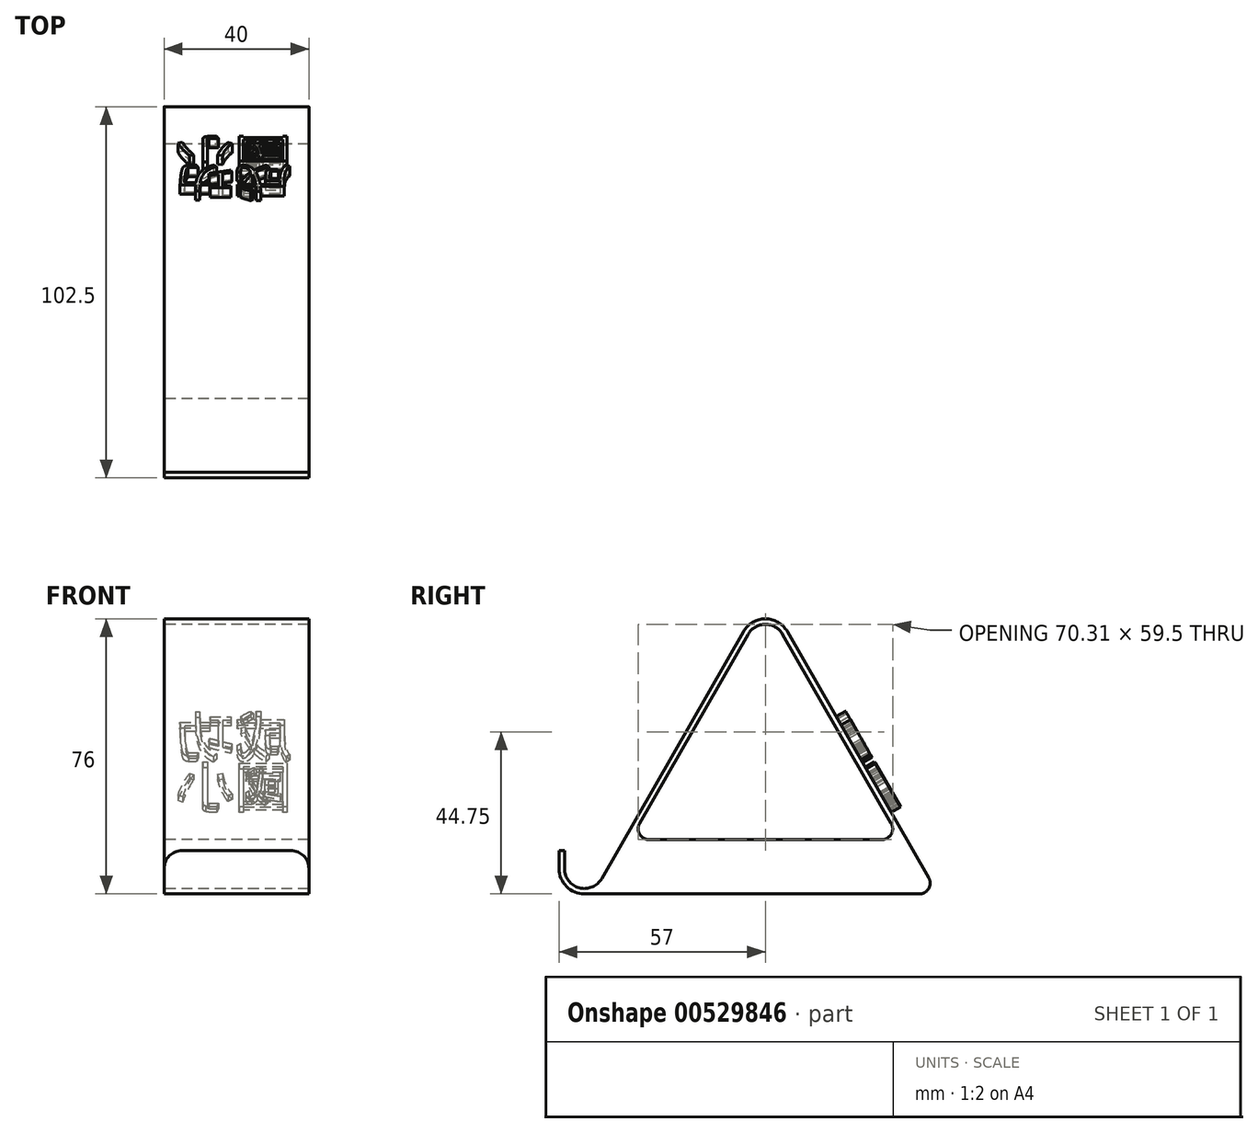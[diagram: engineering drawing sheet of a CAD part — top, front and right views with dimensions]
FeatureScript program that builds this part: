
annotation { "Feature Type Name" : "Feature", "Feature Type Description" : "" }
export const myFeature = defineFeature(function(context is Context, id is Id, definition is map)
    precondition{}
    {
        {
            var Q0;
            Q0=qCreatedBy(makeId("Right.planeOp"),FACE);
            var sketch = newSketch(context, id + "F0", { "sketchPlane" : qUnion([Q0])});
            skArc(sketch, "E0", {"start": v(-7, 0) * mm, "mid": v(-4.95, -4.95) * mm, "end": v(0, -7) * mm});
            skArc(sketch, "E1", {"start": v(54.77, 64.74) * mm, "mid": v(50, 67.5) * mm, "end": v(45.23, 64.74) * mm});
            skLineSegment(sketch, "E2", {"start": v(15.24, 12.5) * mm, "end": v(45.23, 64.74) * mm});
            skLineSegment(sketch, "E3", {"start": v(50, 62) * mm, "end": v(50, -35.11) * mm, "construction": true});
            skLineSegment(sketch, "E4.0.MirrorCS", {"start": v(84.76, 12.5) * mm, "end": v(54.77, 64.74) * mm});
            skLineSegment(sketch, "E5", {"start": v(0, -7) * mm, "end": v(125.8, -7) * mm, "construction": true});
            skLineSegment(sketch, "E6", {"start": v(-7, 0) * mm, "end": v(-7, 5) * mm});
            skLineSegment(sketch, "E7.0", {"start": v(-5.5, 0) * mm, "end": v(-5.5, 5) * mm});
            skArc(sketch, "E7.1", {"start": v(-5.5, 0) * mm, "mid": v(-1.42, -5.31) * mm, "end": v(4.77, -2.74) * mm});
            skLineSegment(sketch, "E7.2", {"start": v(4.77, -2.74) * mm, "end": v(43.93, 65.48) * mm});
            skArc(sketch, "E7.3", {"start": v(56.07, 65.48) * mm, "mid": v(50, 69) * mm, "end": v(43.93, 65.48) * mm});
            skLineSegment(sketch, "E7.4", {"start": v(95.1, -2.5) * mm, "end": v(56.07, 65.48) * mm});
            skLineSegment(sketch, "E8", {"start": v(-7, 5) * mm, "end": v(-5.5, 5) * mm});
            skLineSegment(sketch, "E9", {"start": v(0, -7) * mm, "end": v(92.5, -7) * mm});
            skLineSegment(sketch, "E10.0", {"start": v(17.84, 8) * mm, "end": v(82.16, 8) * mm});
            skPoint(sketch, "E11.visualSharp", {"position": v(12.66, 8) * mm});
            skArc(sketch, "E11.filletArc", {"start": v(15.24, 12.5) * mm, "mid": v(15.25, 9.5) * mm, "end": v(17.84, 8) * mm});
            skPoint(sketch, "E12.visualSharp", {"position": v(87.34, 8) * mm});
            skArc(sketch, "E12.filletArc", {"start": v(82.16, 8) * mm, "mid": v(84.75, 9.5) * mm, "end": v(84.76, 12.5) * mm});
            skPoint(sketch, "E13.visualSharp", {"position": v(97.68, -7) * mm});
            skArc(sketch, "E13.filletArc", {"start": v(92.5, -7) * mm, "mid": v(95.1, -5.5) * mm, "end": v(95.1, -2.5) * mm});
            skSolve(sketch);
        }
        {
            var Q0;
            Q0=makeQuery(id+"F0.imprint","IMPRINT",FACE,{"disambiguationData":[TD([[makeQuery(id+"F0.imprint","IMPRINT",EDGE,{"derivedFrom":sQuery(id+"F0.wireOp",EDGE,"E0")}),1.0]])]});
            extrude(context, id + "F1", {"entities" : qUnion([Q0]), "depth" : 40 * mm});
        }
        {
            var Q0;
            Q0=makeQuery(id+"F1.opExtrude","CAP_EDGE",EDGE,{"disambiguationData":[OSD([sQuery(id+"F0.wireOp",EDGE,"E8")])],"isStart":false});
            var Q1;
            Q1=makeQuery(id+"F1.opExtrude","CAP_EDGE",EDGE,{"disambiguationData":[OSD([sQuery(id+"F0.wireOp",EDGE,"E8")])],"isStart":true});
            fillet(context, id + "F2", {"entities" : qUnion([Q0, Q1]), "radius" : 5 * mm, "tangentPropagation" : true, "allowEdgeOverflow" : false});
        }
        {
            var Q0;
            Q0=sQuery(id+"F0.wireOp",VERTEX,"E7.4.start");
            var Q1;
            Q1=makeQuery(id+"F1.opExtrude","CAP_VERTEX",VERTEX,{"disambiguationData":[OSD([sQuery(id+"F0.wireOp",EDGE,"E7.4"),sQuery(id+"F0.wireOp",EDGE,"E13.filletArc")])],"isStart":false});
            var Q2;
            Q2=sQuery(id+"F0.wireOp",VERTEX,"E7.4.end");
            cPlane(context, id + "F3", {"entities" : qUnion([Q0, Q1, Q2]), "cplaneType" : CPlaneType.THREE_POINT, "offset" : 25 * mm, "width" : 150 * mm, "height" : 150 * mm});
        }
        {
            var Q0;
            Q0=qCreatedBy(id+"F3.planeOp",FACE);
            var sketch = newSketch(context, id + "F4", { "sketchPlane" : qUnion([Q0])});
            skText(sketch, "E14", { "text": "成功\n國小", "fontName": "NotoSansCJKsc-Regular.otf"});
            const initialGuessF4  = {"E14": [-0.03535, -0.0115, 1, 0, 0.0115]};
            skSetInitialGuess(sketch, initialGuessF4);
            skSolve(sketch);
        }
        {
            var Q0;
            Q0 = qSketchRegion(id + "F4", true);
            var Q1;
            Q1=makeQuery(id+"F4.imprint","IMPRINT",FACE,{"disambiguationData":[TD([[makeQuery(id+"F4.imprint","IMPRINT",EDGE,{"derivedFrom":sQuery(id+"F4.wireOp",EDGE,"E14.sketch_text.stroke-88")}),1.0]])]});
            extrude(context, id + "F5", {"entities" : qUnion([Q0, Q1]), "depth" : 3 * mm, "offsetDistance" : 25 * mm});
        }
        {
            var Q0;
            Q0=makeQuery(id+"F4.imprint","IMPRINT",FACE,{"disambiguationData":[TD([[makeQuery(id+"F4.imprint","IMPRINT",EDGE,{"derivedFrom":sQuery(id+"F4.wireOp",EDGE,"E14.sketch_text.stroke-76")}),1.0]])]});
            var Q1;
            Q1=makeQuery(id+"F4.imprint","IMPRINT",FACE,{"disambiguationData":[TD([[makeQuery(id+"F4.imprint","IMPRINT",EDGE,{"derivedFrom":sQuery(id+"F4.wireOp",EDGE,"E14.sketch_text.stroke-72")}),1.0]])]});
            extrude(context, id + "F6", {"entities" : qUnion([Q0, Q1]), "operationType" : NewBodyOperationType.ADD, "depth" : 3 * mm, "offsetDistance" : 25 * mm});
        }
        {
            var Q0;
            Q0 = qSketchRegion(id + "F4", true);
            var Q1;
            Q1=makeQuery(id+"F4.imprint","IMPRINT",FACE,{"disambiguationData":[TD([[makeQuery(id+"F4.imprint","IMPRINT",EDGE,{"derivedFrom":sQuery(id+"F4.wireOp",EDGE,"E14.sketch_text.stroke-80")}),1.0]])]});
            extrude(context, id + "F7", {"entities" : qUnion([Q0, Q1]), "depth" : 3 * mm, "offsetDistance" : 25 * mm});
        }
    });
